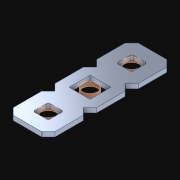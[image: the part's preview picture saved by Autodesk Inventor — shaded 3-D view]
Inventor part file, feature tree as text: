
AUTODESK INVENTOR PART (.ipt)
format: ipt  version: 2021 (Build 250183000, 183)  size: 148,480 bytes
history: native  units: in
note: dims shown in document units (in); Inventor stores cm internally (conversion verified against a paired STEP export)
features: other x4, extrude x3, pattern_linear x1, sketch x1
ambient origin geometry x8: Origin, YZ Plane, XZ Plane, XY Plane, X Axis, Y Axis, Z Axis, Center Point
bodies: Solid1 (feature_tree)
feature tree (9):
  pattern_linear  "Rectangular Pattern1"  Spacing1=1.0in  [1 undecoded]
  sketch  "Sketch1"  dims[d0=0.182in d1=1.0in d2=0.0in d3=1.1811in d5=0.5in]
  other  "Srf1"
  other  "Srf2"
  other  "Srf3"
  parser-record x1  (decoder bookkeeping rows leaked as tree rows — omitted from the tree; the rows remain in map.json)
  extrude  "ExtrusionSrf1"  Depth=0.5in
  extrude  "ExtrusionSrf2"  [1 undecoded]
  extrude  "ExtrusionSrf3"  [1 undecoded]
note: 3 required parameter values undecoded (feature->parameter linkage not recoverable at this tier; creation-order binding heuristic only, values carry confidence <= 0.55)
